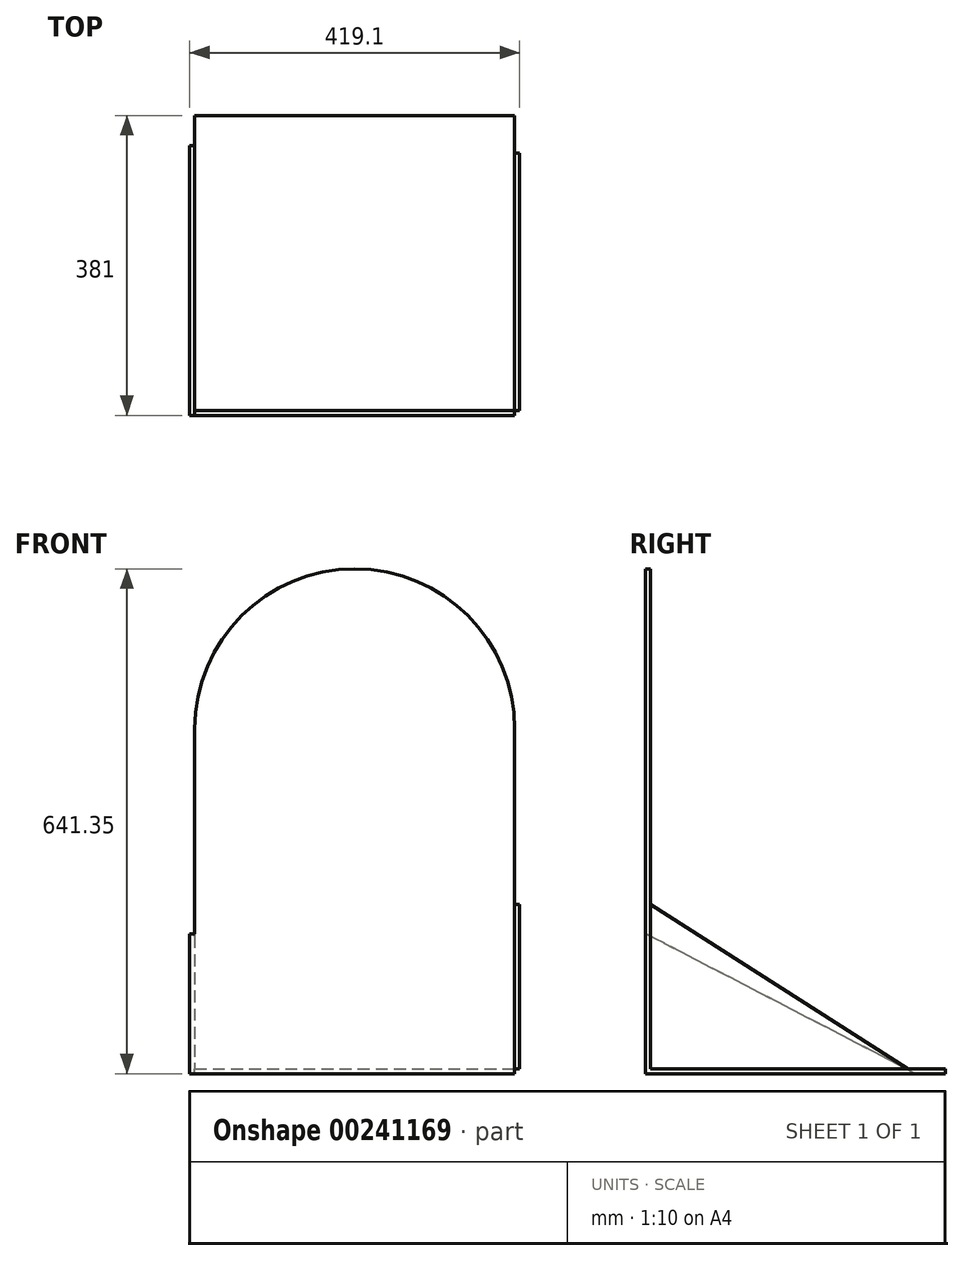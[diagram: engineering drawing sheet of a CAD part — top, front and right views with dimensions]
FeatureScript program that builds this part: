
annotation { "Feature Type Name" : "Feature", "Feature Type Description" : "" }
export const myFeature = defineFeature(function(context is Context, id is Id, definition is map)
    precondition{}
    {
        {
            var Q0;
            Q0=qCreatedBy(makeId("Front.planeOp"),FACE);
            var sketch = newSketch(context, id + "F0", { "sketchPlane" : qUnion([Q0])});
            skLineSegment(sketch, "E0.top", {"start": v(-203.2, -215.9) * mm, "end": v(203.2, -215.9) * mm});
            skLineSegment(sketch, "E0.left", {"start": v(-203.2, 215.9) * mm, "end": v(-203.2, -215.9) * mm});
            skLineSegment(sketch, "E0.right", {"start": v(203.2, 215.9) * mm, "end": v(203.2, -215.9) * mm});
            skPoint(sketch, "E0.middle", {"position": v(0, 0) * mm});
            skArc(sketch, "E1", {"start": v(203.2, 215.9) * mm, "mid": v(0, 419.1) * mm, "end": v(-203.2, 215.9) * mm});
            skLineSegment(sketch, "E2", {"start": v(0, 419.1) * mm, "end": v(0, -215.9) * mm, "construction": true});
            skPoint(sketch, "E3.start.orphan", {"position": v(0, -513.94) * mm});
            skPoint(sketch, "E4.orphan", {"position": v(677.94, -513.94) * mm});
            skSolve(sketch);
        }
        {
            var Q0;
            {var subQ4=sQuery(id+"F0.wireOp",EDGE,"E1");Q0=makeQuery(id+"F0.imprint","IMPRINT",FACE,{"disambiguationData":[TD([[makeQuery(id+"F0.imprint","IMPRINT",EDGE,{"derivedFrom":subQ4}),1.0]])]});}
            extrude(context, id + "F1", {"entities" : qUnion([Q0]), "depth" : 6.35 * mm});
        }
        {
            var Q0;
            Q0=makeQuery(id+"F1.opExtrude","SWEPT_FACE",FACE,{"disambiguationData":[OSD([sQuery(id+"F0.wireOp",EDGE,"E0.top")])]});
            cPlane(context, id + "F2", {"entities" : qUnion([Q0]), "cplaneType" : CPlaneType.OFFSET, "offset" : 0 * mm, "width" : 152.4 * mm, "height" : 152.4 * mm});
        }
        {
            var Q0;
            Q0=qCreatedBy(id+"F2.planeOp",FACE);
            var sketch = newSketch(context, id + "F3", { "sketchPlane" : qUnion([Q0])});
            skLineSegment(sketch, "E5.bottom", {"start": v(-203.2, 6.35) * mm, "end": v(203.2, 6.35) * mm});
            skLineSegment(sketch, "E5.top", {"start": v(-203.2, -374.65) * mm, "end": v(203.2, -374.65) * mm});
            skLineSegment(sketch, "E5.left", {"start": v(-203.2, 6.35) * mm, "end": v(-203.2, -374.65) * mm});
            skLineSegment(sketch, "E5.right", {"start": v(203.2, 6.35) * mm, "end": v(203.2, -374.65) * mm});
            skLineSegment(sketch, "E6", {"start": v(0, -374.65) * mm, "end": v(0, 0.22) * mm, "construction": true});
            skPoint(sketch, "E6.endSnap0", {"position": v(0, 6.35) * mm});
            skSolve(sketch);
        }
        {
            var Q0;
            Q0=makeQuery(id+"F3.imprint","IMPRINT",FACE,{"disambiguationData":[TD([[makeQuery(id+"F3.imprint","IMPRINT",EDGE,{"derivedFrom":sQuery(id+"F3.wireOp",EDGE,"E5.bottom")}),-1.0]])]});
            extrude(context, id + "F4", {"entities" : qUnion([Q0]), "operationType" : NewBodyOperationType.ADD, "depth" : 6.35 * mm});
        }
        {
            var Q0;
            Q0=makeQuery(id+"F4.boolean.opBoolean","MERGE",FACE,{"derivedFrom":[makeQuery(id+"F1.opExtrude","SWEPT_FACE",FACE,{"disambiguationData":[OSD([sQuery(id+"F0.wireOp",EDGE,"E0.left")])]}),makeQuery(id+"F4.opExtrude","SWEPT_FACE",FACE,{"disambiguationData":[OSD([sQuery(id+"F3.wireOp",EDGE,"E5.left")])]})]});
            cPlane(context, id + "F5", {"entities" : qUnion([Q0]), "cplaneType" : CPlaneType.OFFSET, "offset" : 0 * mm, "width" : 152.4 * mm, "height" : 152.4 * mm});
        }
        {
            var Q0;
            Q0=qCreatedBy(id+"F5.planeOp",FACE);
            var sketch = newSketch(context, id + "F6", { "sketchPlane" : qUnion([Q0])});
            skLineSegment(sketch, "E7", {"start": v(-336.55, -222.25) * mm, "end": v(6.35, -44.45) * mm});
            skLineSegment(sketch, "E8", {"start": v(6.35, -44.45) * mm, "end": v(6.35, -222.25) * mm});
            skLineSegment(sketch, "E9", {"start": v(6.35, -222.25) * mm, "end": v(-336.55, -222.25) * mm});
            skSolve(sketch);
        }
        {
            var Q0;
            Q0=makeQuery(id+"F6.imprint","IMPRINT",FACE,{"disambiguationData":[TD([[makeQuery(id+"F6.imprint","IMPRINT",EDGE,{"derivedFrom":sQuery(id+"F6.wireOp",EDGE,"E7")}),-1.0]])]});
            extrude(context, id + "F7", {"entities" : qUnion([Q0]), "operationType" : NewBodyOperationType.ADD, "depth" : 6.35 * mm});
        }
        {
            var Q0;
            Q0=makeQuery(id+"F4.boolean.opBoolean","MERGE",FACE,{"derivedFrom":[makeQuery(id+"F1.opExtrude","SWEPT_FACE",FACE,{"disambiguationData":[OSD([sQuery(id+"F0.wireOp",EDGE,"E0.right")])]}),makeQuery(id+"F4.opExtrude","SWEPT_FACE",FACE,{"disambiguationData":[OSD([sQuery(id+"F3.wireOp",EDGE,"E5.right")])]})]});
            var sketch = newSketch(context, id + "F8", { "sketchPlane" : qUnion([Q0])});
            skLineSegment(sketch, "E10", {"start": v(-6.35, -222.25) * mm, "end": v(336.55, -222.25) * mm});
            skLineSegment(sketch, "E11", {"start": v(-6.35, -222.25) * mm, "end": v(-6.35, -3.18) * mm});
            skLineSegment(sketch, "E12", {"start": v(-6.35, -3.17) * mm, "end": v(336.55, -222.25) * mm});
            skPoint(sketch, "E13", {"position": v(-6.35, -3.17) * mm});
            skSolve(sketch);
        }
        {
            var Q0;
            {var subQ0=sQuery(id+"F8.wireOp",EDGE,"E11");var subQ1=makeQuery(id+"F4.opExtrude","CAP_EDGE",EDGE,{"disambiguationData":[OSD([sQuery(id+"F3.wireOp",EDGE,"E5.right")])],"isStart":true});var subQ2=makeQuery(id+"F8.imprint","INTERSECT",VERTEX,{"derivedFrom":[subQ1,subQ0]});Q0=makeQuery(id+"F8.imprint","IMPRINT",FACE,{"disambiguationData":[TD([[makeQuery(id+"F8.imprint","IMPRINT",EDGE,{"disambiguationData":[TD([[subQ2,-1.0]])],"derivedFrom":subQ0}),-1.0]])]});}
            var Q1;
            {var subQ0=sQuery(id+"F8.wireOp",EDGE,"E12");var subQ1=makeQuery(id+"F1.opExtrude","CAP_EDGE",EDGE,{"disambiguationData":[OSD([sQuery(id+"F0.wireOp",EDGE,"E0.right")])],"isStart":true});var subQ2=makeQuery(id+"F8.imprint","INTERSECT",VERTEX,{"derivedFrom":[subQ1,subQ0]});Q1=makeQuery(id+"F8.imprint","IMPRINT",FACE,{"disambiguationData":[TD([[makeQuery(id+"F8.imprint","IMPRINT",EDGE,{"disambiguationData":[TD([[subQ2,-1.0]])],"derivedFrom":subQ0}),-1.0]])]});}
            extrude(context, id + "F9", {"entities" : qUnion([Q0, Q1]), "depth" : 6.35 * mm});
        }
    });
